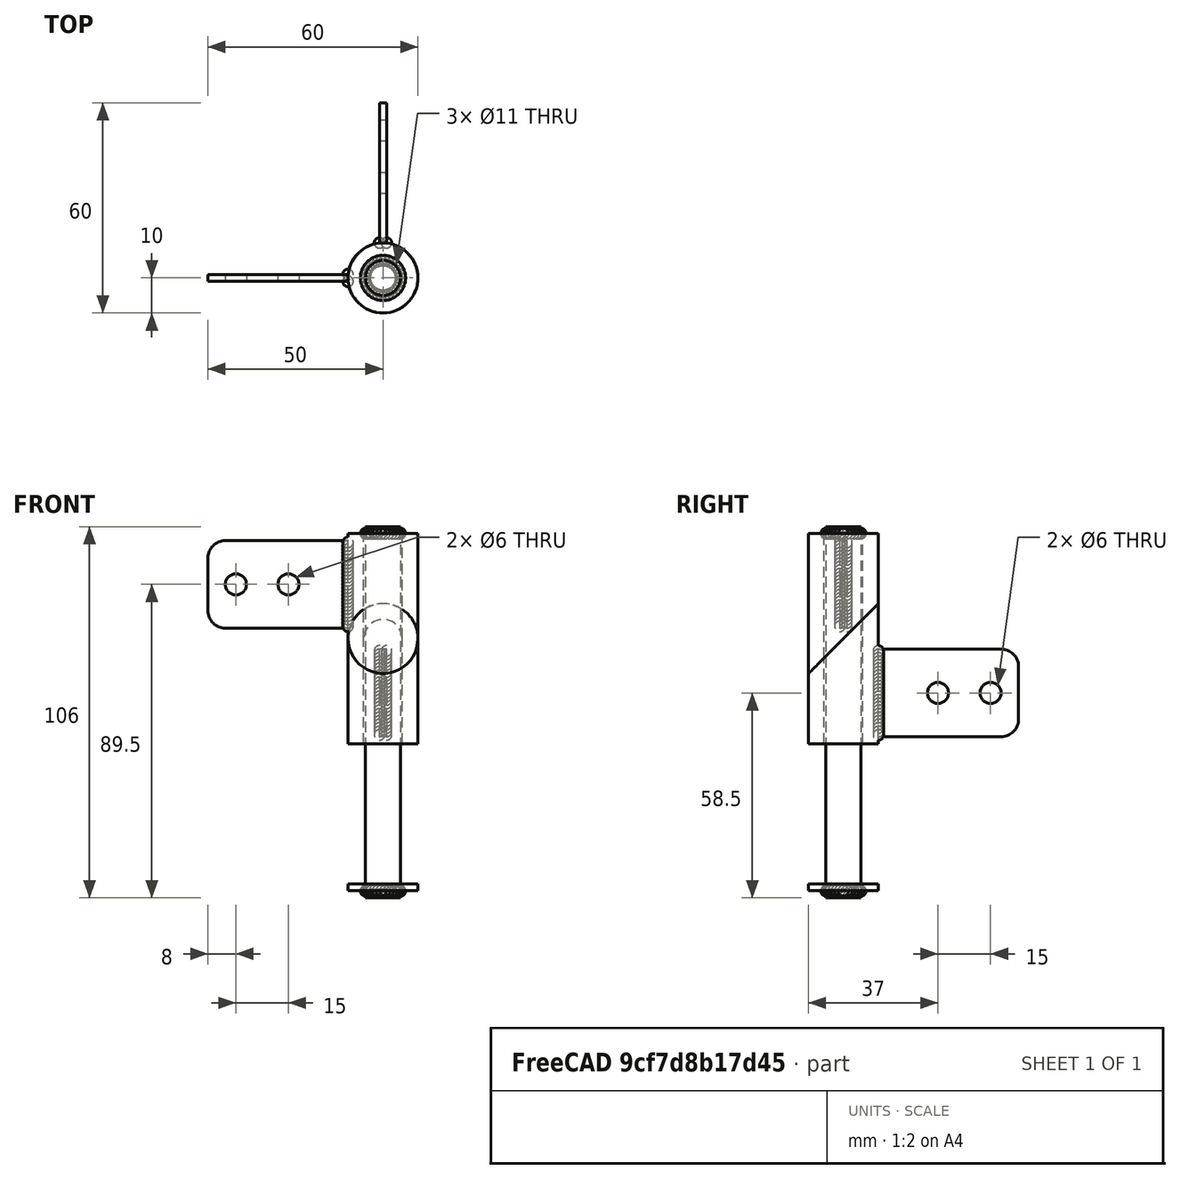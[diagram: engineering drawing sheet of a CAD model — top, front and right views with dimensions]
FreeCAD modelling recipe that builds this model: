
FCSTD DOCUMENT  (FreeCAD 0.18R16093 +53 (Git))
Label: FREECAD 209 - SPRING HINGE
License: All rights reserved
LicenseURL: http://en.wikipedia.org/wiki/All_rights_reserved
objects: Part::FeaturePython×9, Part::Compound×4, Part::Cylinder×3, App::DocumentObjectGroupPython×3, Part::Sphere×2, Part::Plane×1, App::DocumentObjectGroup×1, Part::Box×1, Part::Fillet×1, Part::Cut×1, Part::Helix×1, Spreadsheet::Sheet×1
note: 23 computed .brp shape members not serialized (recipe doc carries the construction recipe); baked Part::Feature solids carry a one-line shape summary decoded from their .brp

FEATURE [Part::FeaturePython] Tube  # WARN: FeaturePython — macro-defined, semantics opaque (R4)
  Height = 60
  InnerRadius = 5.5
  OuterRadius = 10
  Placement = pos=(0,0,-30) rot=(0,0,1;0rad)
FEATURE [Part::Plane] Plane
  AttacherType = Attacher::AttachEngine3D
  Length = 30
  Placement = pos=(-15,-10.6066,-10.6066) rot=(1,0,0;0.785398rad)
  Width = 30
FEATURE [Part::FeaturePython] Slice  # WARN: FeaturePython — macro-defined, semantics opaque (R4)
  Base = -> Tube
  Mode = 1
  Tolerance = 0
  Tools = -> [Plane]
FEATURE [Part::FeaturePython] Slice_child0  label="Slice.0"  # WARN: FeaturePython — macro-defined, semantics opaque (R4)
  Base = -> Slice
  FilterType = 1
  Invert = false
  OverrideMaxVal = 0
  WindowFrom = 80
  WindowTo = 100
  items = 0
FEATURE [Part::FeaturePython] Slice_child1  label="Slice.1"  # WARN: FeaturePython — macro-defined, semantics opaque (R4)
  Base = -> Slice
  FilterType = 1
  Invert = false
  OverrideMaxVal = 0
  WindowFrom = 80
  WindowTo = 100
  items = 1
FEATURE [App::DocumentObjectGroup] GrExplode_Slice  label="Exploded Slice"
  Group = -> [Slice_child0,Slice_child1]
FEATURE [Part::Cylinder] Cylinder
  Angle = 360
  AttacherType = Attacher::AttachEngine3D
  Height = 106
  Placement = pos=(0,3.9e-15,32) rot=(1,0,0;3.14159rad)
  Radius = 5
FEATURE [Part::Sphere] Sphere
  Angle1 = -90
  Angle2 = 90
  Angle3 = 360
  AttacherType = Attacher::AttachEngine3D
  Placement = pos=(-5,0,30) rot=(0,0,1;0rad)
  Radius = 1.5
FEATURE [Part::FeaturePython] Array  # Draft array (typed FeaturePython)
  Angle = 360
  ArrayType = 1
  Axis = (0,0,1)
  Base = -> Sphere
  Center = (0,0,0)
  Fuse = false
  IntervalAxis = (0,0,0)
  IntervalX = (1,0,0)
  IntervalY = (0,1,0)
  IntervalZ = (0,0,1)
  NumberPolar = 30
  NumberX = 2
  NumberY = 2
  NumberZ = 1
FEATURE [Part::FeaturePython] Tube001  # WARN: FeaturePython — macro-defined, semantics opaque (R4)
  Height = 2
  InnerRadius = 5.5
  OuterRadius = 10
  Placement = pos=(0,0,-72) rot=(0,0,1;0rad)
FEATURE [Part::FeaturePython] Clone  label="Array001"  # Draft clone (typed FeaturePython)
  AttacherType = Attacher::AttachEngine3D
  Fuse = false
  Objects = -> [Array]
  Placement = pos=(0,-5.1e-15,-42) rot=(1,0,0;3.14159rad)
  Scale = (1,1,1)
FEATURE [Part::Box] Box  label="Cube"
  AttacherType = Attacher::AttachEngine3D
  Height = 25
  Length = 40
  Placement = pos=(0,-1,0) rot=(0,0,1;0rad)
  Width = 2
FEATURE [Part::Fillet] Fillet
  Base = -> Box
  Edges = 2 edges r=5: [Edge6,Edge8]
FEATURE [Part::Cylinder] Cylinder001
  Angle = 360
  AttacherType = Attacher::AttachEngine3D
  Height = 10
  Placement = pos=(32,-5,12.5) rot=(1,0,0;4.71239rad)
  Radius = 3
FEATURE [Part::Cylinder] Cylinder002
  Angle = 360
  AttacherType = Attacher::AttachEngine3D
  Height = 10
  Placement = pos=(17,-5,12.5) rot=(-1,0,0;1.5708rad)
  Radius = 3
FEATURE [Part::Compound] Compound
  Links = -> [Cylinder002,Cylinder001]
FEATURE [Part::Cut] Cut
  Base = -> Fillet
  Placement = pos=(10,0,3) rot=(0,0,1;0rad)
  Tool = -> Compound
FEATURE [Part::Sphere] Sphere001
  Angle1 = -90
  Angle2 = 90
  Angle3 = 360
  AttacherType = Attacher::AttachEngine3D
  Placement = pos=(10,-1,3.5) rot=(0,0,1;0rad)
  Radius = 1.5
FEATURE [Part::FeaturePython] Array001  label="Array002"  # Draft array (typed FeaturePython)
  Angle = 360
  ArrayType = 0
  Axis = (0,0,1)
  Base = -> Sphere001
  Center = (0,0,0)
  Fuse = false
  IntervalAxis = (0,0,0)
  IntervalX = (1,0,0)
  IntervalY = (0,2,0)
  IntervalZ = (0,0,1)
  NumberPolar = 1
  NumberX = 1
  NumberY = 2
  NumberZ = 25
FEATURE [Part::Compound] Compound001
  Links = -> [Cut,Array001]
  Placement = pos=(0,0,0) rot=(0,0,1;3.14159rad)
FEATURE [Part::FeaturePython] Clone001  label="Compound002"  # Draft clone (typed FeaturePython)
  AttacherType = Attacher::AttachEngine3D
  Fuse = false
  Objects = -> [Compound001]
  Placement = pos=(0,0,-31) rot=(0,0,1;1.5708rad)
  Scale = (1,1,1)
FEATURE [Part::Compound] Compound002  label="Compound003"
  Links = -> [Slice_child1,Clone001]
FEATURE [Part::Compound] Compound003  label="Compound004"
  Links = -> [Compound001,Clone,Tube001,Array,Cylinder,Slice_child0]
FEATURE [Part::Helix] Helix
  Angle = 0
  AttacherType = Attacher::AttachEngine3D
  Height = 40
  LocalCoord = 0
  Pitch = 10
  Placement = pos=(0,0,-70) rot=(0,0,1;0rad)
  Radius = 8
  Style = 1
  expr: Height = Spreadsheet.height
  expr: Pitch = Spreadsheet.step
FEATURE [App::DocumentObjectGroupPython] My_Placer  # scripted group (container) (typed FeaturePython)
  RotAxis = (0,0,1)
  RotCenter = (0,0,0)
  arc = -time*90
  arc0 = 0
  arc1 = 90
  target = -> Compound003
  time = 0
  x = 0
  x0 = 0
  x1 = 200
  y = 0
  y0 = 0
  y1 = 0
  z = 0
  z0 = 0
  z1 = 0
FEATURE [App::DocumentObjectGroupPython] My_Placer001  # scripted group (container) (typed FeaturePython)
  RotAxis = (0,0,1)
  RotCenter = (0,0,0)
  arc = 0
  arc0 = 0
  arc1 = 90
  target = -> Compound002
  time = 0
  x = 0
  x0 = 0
  x1 = 200
  y = 0
  y0 = 0
  y1 = 0
  z = -time*14
  z0 = 0
  z1 = 0
FEATURE [App::DocumentObjectGroupPython] My_Manager  # scripted group (container) (typed FeaturePython)
  Group = -> [My_Placer,My_Placer001]
  intervall = 100
  sleeptime = 0.02
  start = 0
  step = 0
  text = NO
FEATURE [Spreadsheet::Sheet] Spreadsheet
  cells = A1=step; B1(step)==10 - 10 * C1; C1==My_Manager.step * 0.0035; A2=height; B2(height)==40 - 40 * C1
